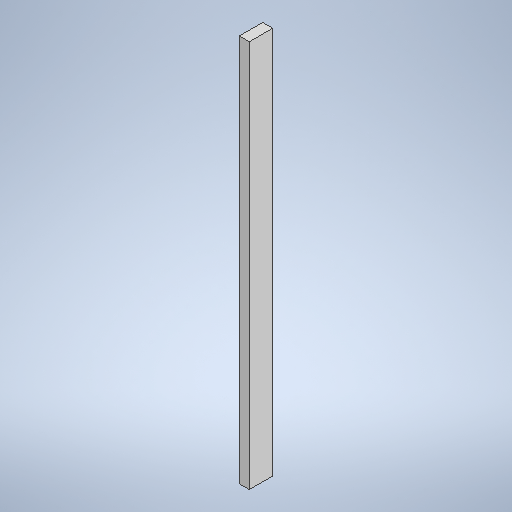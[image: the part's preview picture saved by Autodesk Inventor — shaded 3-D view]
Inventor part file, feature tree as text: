
AUTODESK INVENTOR PART (.ipt)
format: ipt  version: 2025 (Build 290162000, 162)  size: 247,296 bytes
history: native  units: in
note: dims shown in document units (in); Inventor stores cm internally (conversion verified against a paired STEP export)
features: extrude x1, sketch x1
ambient origin geometry x8: Origin, YZ Plane, XZ Plane, XY Plane, X Axis, Y Axis, Z Axis, Center Point
bodies: Solid1 (feature_tree)
feature tree (2):
  extrude  "Extrusion1"  Depth=3.5in
  sketch  "Sketch1"  dims[d0=58.0in d1=3.5in d2=1.5in d3=0.0in]
